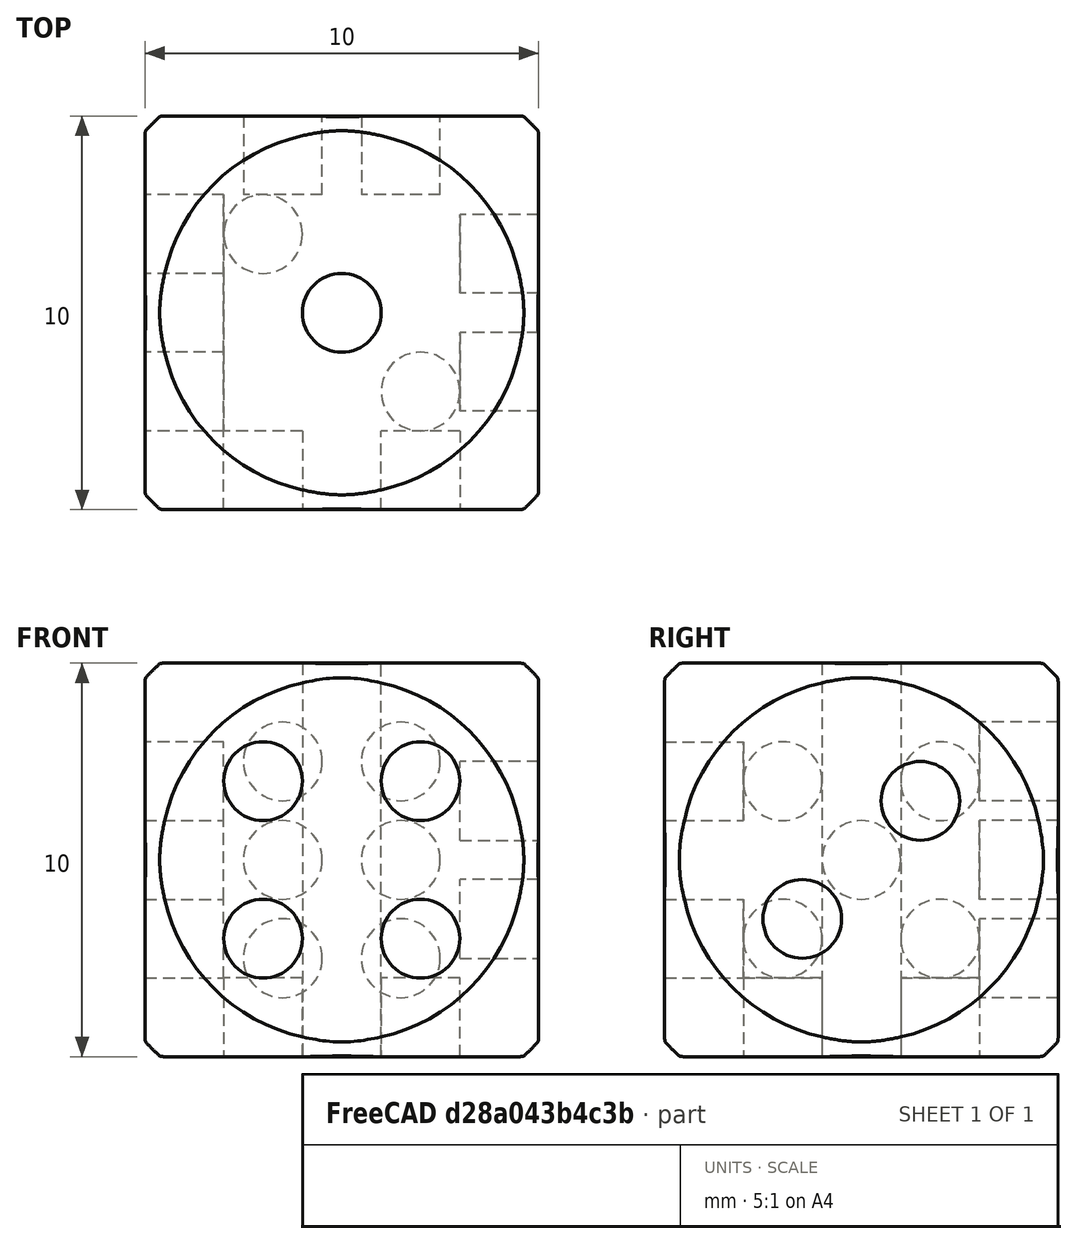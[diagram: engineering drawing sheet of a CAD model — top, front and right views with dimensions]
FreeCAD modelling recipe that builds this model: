
FCSTD DOCUMENT  (FreeCAD 0.21R33694 (Git))
Label: cartacho_exercici2
License: All rights reserved
LicenseURL: http://en.wikipedia.org/wiki/All_rights_reserved
objects: Part::Cylinder×20, Part::Box×1, Part::Sphere×1, Part::Fillet×1, Part::MultiCommon×1
note: 24 computed .brp shape members not serialized (recipe doc carries the construction recipe); baked Part::Feature solids carry a one-line shape summary decoded from their .brp

FEATURE [Part::Box] Box  label="Cube"
  AttacherType = Attacher::AttachEngine3D
  Height = 10
  Length = 10
  Width = 10
FEATURE [Part::Sphere] Sphere
  Angle1 = -90
  Angle2 = 90
  Angle3 = 360
  AttacherType = Attacher::AttachEngine3D
  Placement = pos=(5,5,5) rot=(0,0,1;0rad)
  Radius = 6.8
FEATURE [Part::Fillet] Fillet
  Base = -> Box
  Edges = 12 edges r=0.5: [Edge1,Edge2,Edge3,Edge4,Edge5,Edge6,Edge7,Edge8,Edge9,Edge10,Edge11,Edge12]
FEATURE [Part::MultiCommon] Common
  Refine = true
  Shapes = -> [Fillet,Sphere]
FEATURE [Part::Cylinder] Cylinder
  Angle = 360
  AttacherType = Attacher::AttachEngine3D
  FirstAngle = 0
  Height = 10
  Placement = pos=(5,5,0) rot=(0,0,1;0rad)
  Radius = 1
  SecondAngle = 0
FEATURE [Part::Cylinder] Cylinder001
  Angle = 360
  AttacherType = Attacher::AttachEngine3D
  FirstAngle = 0
  Height = 2
  Placement = pos=(7,3,0) rot=(0,0,1;0rad)
  Radius = 1
  SecondAngle = 0
FEATURE [Part::Cylinder] Cylinder002
  Angle = 360
  AttacherType = Attacher::AttachEngine3D
  FirstAngle = 0
  Height = 2
  Placement = pos=(3,7,0) rot=(0,0,1;0rad)
  Radius = 1
  SecondAngle = 0
FEATURE [Part::Cylinder] Cylinder003
  Angle = 360
  AttacherType = Attacher::AttachEngine3D
  FirstAngle = 0
  Height = 2
  Placement = pos=(0,5,5) rot=(0,1,0;1.5708rad)
  Radius = 1
  SecondAngle = 0
FEATURE [Part::Cylinder] Cylinder004
  Angle = 360
  AttacherType = Attacher::AttachEngine3D
  FirstAngle = 0
  Height = 2
  Placement = pos=(0,7,7) rot=(0,1,0;1.5708rad)
  Radius = 1
  SecondAngle = 0
FEATURE [Part::Cylinder] Cylinder005
  Angle = 360
  AttacherType = Attacher::AttachEngine3D
  FirstAngle = 0
  Height = 2
  Placement = pos=(0,7,3) rot=(0,1,0;1.5708rad)
  Radius = 1
  SecondAngle = 0
FEATURE [Part::Cylinder] Cylinder006
  Angle = 360
  AttacherType = Attacher::AttachEngine3D
  FirstAngle = 0
  Height = 2
  Placement = pos=(0,3,7) rot=(0,1,0;1.5708rad)
  Radius = 1
  SecondAngle = 0
FEATURE [Part::Cylinder] Cylinder007
  Angle = 360
  AttacherType = Attacher::AttachEngine3D
  FirstAngle = 0
  Height = 2
  Placement = pos=(0,3,3) rot=(0,1,0;1.5708rad)
  Radius = 1
  SecondAngle = 0
FEATURE [Part::Cylinder] Cylinder008
  Angle = 360
  AttacherType = Attacher::AttachEngine3D
  FirstAngle = 0
  Height = 2
  Placement = pos=(3,2,3) rot=(1,0,0;1.5708rad)
  Radius = 1
  SecondAngle = 0
FEATURE [Part::Cylinder] Cylinder009
  Angle = 360
  AttacherType = Attacher::AttachEngine3D
  FirstAngle = 0
  Height = 2
  Placement = pos=(7,2,3) rot=(1,0,0;1.5708rad)
  Radius = 1
  SecondAngle = 0
FEATURE [Part::Cylinder] Cylinder010
  Angle = 360
  AttacherType = Attacher::AttachEngine3D
  FirstAngle = 0
  Height = 2
  Placement = pos=(7,2,7) rot=(1,0,0;1.5708rad)
  Radius = 1
  SecondAngle = 0
FEATURE [Part::Cylinder] Cylinder011
  Angle = 360
  AttacherType = Attacher::AttachEngine3D
  FirstAngle = 0
  Height = 2
  Placement = pos=(3,2,7) rot=(1,0,0;1.5708rad)
  Radius = 1
  SecondAngle = 0
FEATURE [Part::Cylinder] Cylinder012
  Angle = 360
  AttacherType = Attacher::AttachEngine3D
  FirstAngle = 0
  Height = 2
  Placement = pos=(8,3.5,3.5) rot=(0,1,0;1.5708rad)
  Radius = 1
  SecondAngle = 0
FEATURE [Part::Cylinder] Cylinder013
  Angle = 360
  AttacherType = Attacher::AttachEngine3D
  FirstAngle = 0
  Height = 2
  Placement = pos=(8,6.5,6.5) rot=(0,1,0;1.5708rad)
  Radius = 1
  SecondAngle = 0
FEATURE [Part::Cylinder] Cylinder015
  Angle = 360
  AttacherType = Attacher::AttachEngine3D
  FirstAngle = 0
  Height = 2
  Placement = pos=(6.5,8,7.5) rot=(-1,0,0;1.5708rad)
  Radius = 1
  SecondAngle = 0
FEATURE [Part::Cylinder] Cylinder016
  Angle = 360
  AttacherType = Attacher::AttachEngine3D
  FirstAngle = 0
  Height = 2
  Placement = pos=(6.5,8,5) rot=(-1,0,0;1.5708rad)
  Radius = 1
  SecondAngle = 0
FEATURE [Part::Cylinder] Cylinder017
  Angle = 360
  AttacherType = Attacher::AttachEngine3D
  FirstAngle = 0
  Height = 2
  Placement = pos=(6.5,8,2.5) rot=(-1,0,0;1.5708rad)
  Radius = 1
  SecondAngle = 0
FEATURE [Part::Cylinder] Cylinder018
  Angle = 360
  AttacherType = Attacher::AttachEngine3D
  FirstAngle = 0
  Height = 2
  Placement = pos=(3.5,8,7.5) rot=(-1,0,0;1.5708rad)
  Radius = 1
  SecondAngle = 0
FEATURE [Part::Cylinder] Cylinder019
  Angle = 360
  AttacherType = Attacher::AttachEngine3D
  FirstAngle = 0
  Height = 2
  Placement = pos=(3.5,8,5) rot=(-1,0,0;1.5708rad)
  Radius = 1
  SecondAngle = 0
FEATURE [Part::Cylinder] Cylinder020
  Angle = 360
  AttacherType = Attacher::AttachEngine3D
  FirstAngle = 0
  Height = 2
  Placement = pos=(3.5,8,2.5) rot=(-1,0,0;1.5708rad)
  Radius = 1
  SecondAngle = 0
